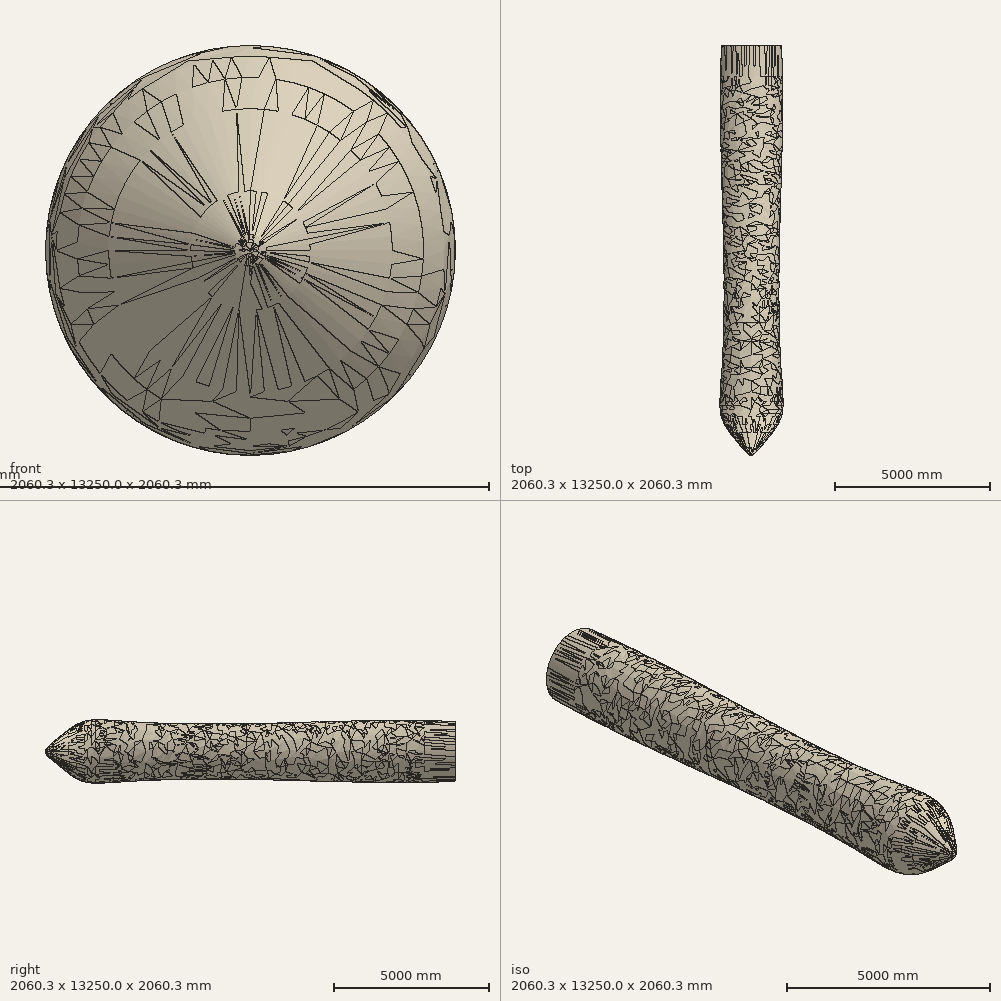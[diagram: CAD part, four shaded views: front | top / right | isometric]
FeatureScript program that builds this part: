
annotation { "Feature Type Name" : "Feature", "Feature Type Description" : "" }
export const myFeature = defineFeature(function(context is Context, id is Id, definition is map)
    precondition{}
    {
        {
            var Q0;
            Q0=qCreatedBy(makeId("Front.planeOp"),FACE);
            var sketch = newSketch(context, id + "F0", { "sketchPlane" : qUnion([Q0])});
            skCircle(sketch, "E0", {"center": v(0, 0) * mm, "radius": 1000 * mm});
            skSolve(sketch);
        }
        {
            var Q0;
            Q0=qCreatedBy(makeId("Front.planeOp"),FACE);
            cPlane(context, id + "F1", {"entities" : qUnion([Q0]), "cplaneType" : CPlaneType.OFFSET, "offset" : 1000 * mm, "width" : 150 * mm, "height" : 150 * mm});
        }
        {
            var Q0;
            Q0=qCreatedBy(id+"F1.planeOp",FACE);
            var sketch = newSketch(context, id + "F2", { "sketchPlane" : qUnion([Q0])});
            skCircle(sketch, "E1", {"center": v(0, 0) * mm, "radius": 976.33 * mm});
            skSolve(sketch);
        }
        {
            var Q0;
            Q0=qCreatedBy(makeId("Front.planeOp"),FACE);
            cPlane(context, id + "F3", {"entities" : qUnion([Q0]), "cplaneType" : CPlaneType.OFFSET, "offset" : 10000 * mm, "oppositeDirection" : true, "width" : 150 * mm, "height" : 150 * mm});
        }
        {
            var Q0;
            Q0=qCreatedBy(id+"F3.planeOp",FACE);
            var sketch = newSketch(context, id + "F4", { "sketchPlane" : qUnion([Q0])});
            skCircle(sketch, "E2", {"center": v(0, 0) * mm, "radius": 1000 * mm});
            skSolve(sketch);
        }
        {
            var Q0;
            Q0=qCreatedBy(id+"F3.planeOp",FACE);
            cPlane(context, id + "F5", {"entities" : qUnion([Q0]), "cplaneType" : CPlaneType.OFFSET, "offset" : 1000 * mm, "oppositeDirection" : true, "width" : 150 * mm, "height" : 150 * mm});
        }
        {
            var Q0;
            Q0=qCreatedBy(id+"F5.planeOp",FACE);
            var sketch = newSketch(context, id + "F6", { "sketchPlane" : qUnion([Q0])});
            skCircle(sketch, "E3", {"center": v(0, 0) * mm, "radius": 975.23 * mm});
            skSolve(sketch);
        }
        {
            var Q0;
            Q0=qCreatedBy(id+"F1.planeOp",FACE);
            cPlane(context, id + "F7", {"entities" : qUnion([Q0]), "cplaneType" : CPlaneType.OFFSET, "offset" : 1000 * mm, "width" : 150 * mm, "height" : 150 * mm});
        }
        {
            var Q0;
            Q0=qCreatedBy(id+"F7.planeOp",FACE);
            var sketch = newSketch(context, id + "F8", { "sketchPlane" : qUnion([Q0])});
            skCircle(sketch, "E4", {"center": v(0, 0) * mm, "radius": 300 * mm});
            skSolve(sketch);
        }
        {
            var Q0;
            Q0=qCreatedBy(id+"F7.planeOp",FACE);
            cPlane(context, id + "F9", {"entities" : qUnion([Q0]), "cplaneType" : CPlaneType.OFFSET, "offset" : 250 * mm, "width" : 150 * mm, "height" : 150 * mm});
        }
        {
            var Q0;
            Q0=qCreatedBy(id+"F9.planeOp",FACE);
            var sketch = newSketch(context, id + "F10", { "sketchPlane" : qUnion([Q0])});
            skCircle(sketch, "E5", {"center": v(0, 0) * mm, "radius": 5 * mm});
            skSolve(sketch);
        }
        {
            var Q0;
            Q0=makeQuery(id+"F10.imprint","IMPRINT",FACE,{"disambiguationData":[TD([[makeQuery(id+"F10.imprint","IMPRINT",EDGE,{"derivedFrom":sQuery(id+"F10.wireOp",EDGE,"E5")}),1.0]])]});
            var Q1;
            Q1=makeQuery(id+"F8.imprint","IMPRINT",FACE,{"disambiguationData":[TD([[makeQuery(id+"F8.imprint","IMPRINT",EDGE,{"derivedFrom":sQuery(id+"F8.wireOp",EDGE,"E4")}),1.0]])]});
            var Q2;
            Q2=makeQuery(id+"F2.imprint","IMPRINT",FACE,{"disambiguationData":[TD([[makeQuery(id+"F2.imprint","IMPRINT",EDGE,{"derivedFrom":sQuery(id+"F2.wireOp",EDGE,"E1")}),1.0]])]});
            var Q3;
            Q3=makeQuery(id+"F0.imprint","IMPRINT",FACE,{"disambiguationData":[TD([[makeQuery(id+"F0.imprint","IMPRINT",EDGE,{"derivedFrom":sQuery(id+"F0.wireOp",EDGE,"E0")}),1.0]])]});
            var Q4;
            Q4=makeQuery(id+"F4.imprint","IMPRINT",FACE,{"disambiguationData":[TD([[makeQuery(id+"F4.imprint","IMPRINT",EDGE,{"derivedFrom":sQuery(id+"F4.wireOp",EDGE,"E2")}),1.0]])]});
            var Q5;
            Q5=makeQuery(id+"F6.imprint","IMPRINT",FACE,{"disambiguationData":[TD([[makeQuery(id+"F6.imprint","IMPRINT",EDGE,{"derivedFrom":sQuery(id+"F6.wireOp",EDGE,"E3")}),1.0]])]});
            loft(context, id + "F11", {"startCondition" : LoftEndDerivativeType.TANGENT_TO_PROFILE, "startMagnitude" : 1, "sheetProfilesArray" : [{ "sheetProfileEntities" : qUnion([Q0]) }, { "sheetProfileEntities" : qUnion([Q1]) }, { "sheetProfileEntities" : qUnion([Q2]) }, { "sheetProfileEntities" : qUnion([Q3]) }, { "sheetProfileEntities" : qUnion([Q4]) }, { "sheetProfileEntities" : qUnion([Q5]) }]});
        }
    });
